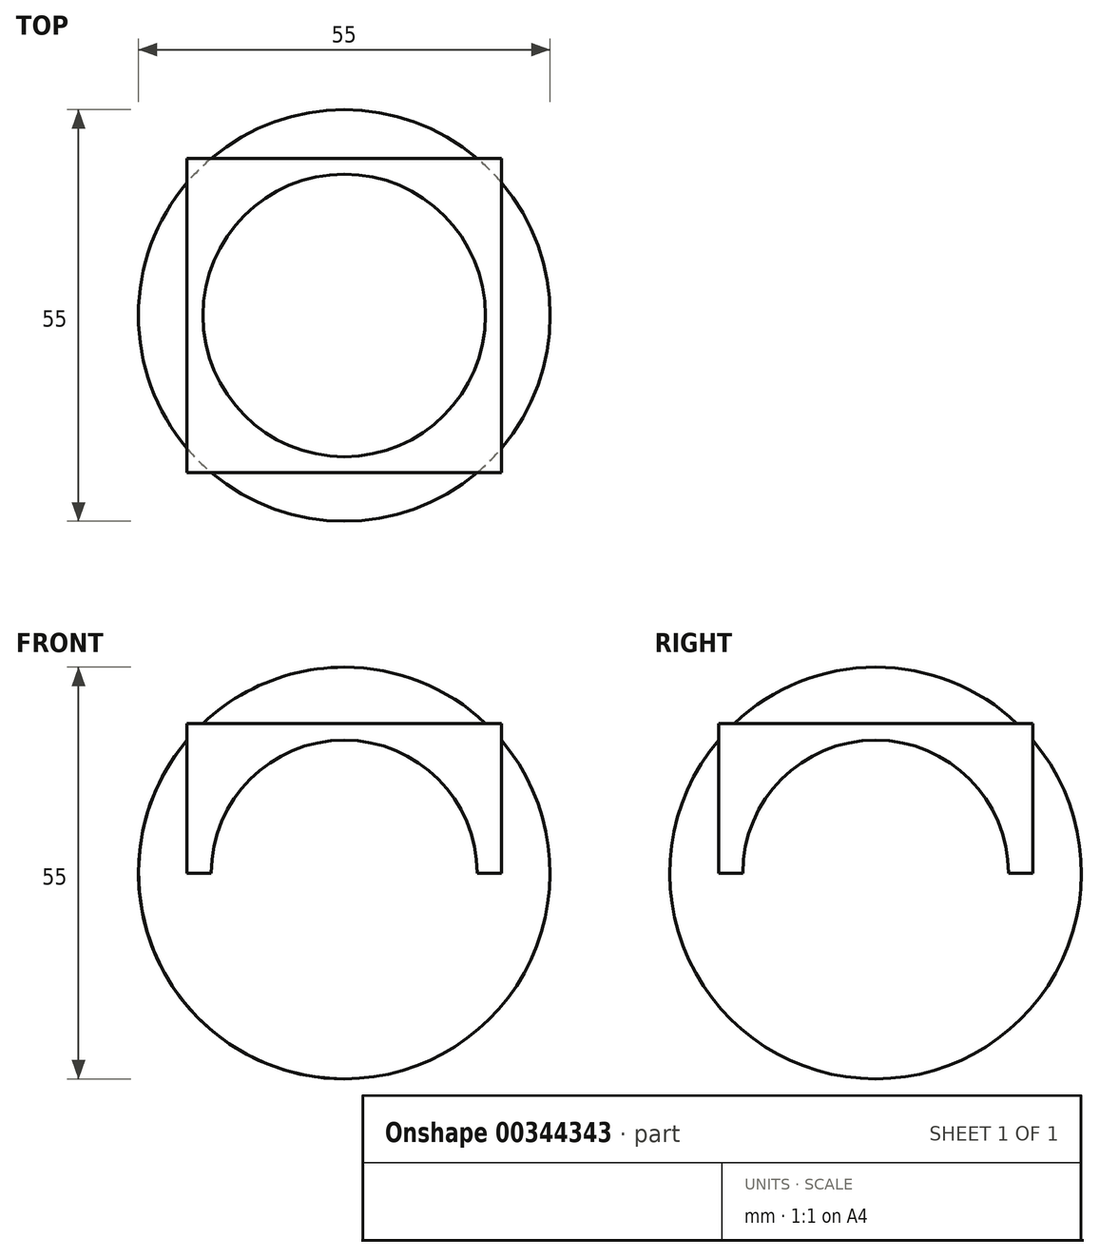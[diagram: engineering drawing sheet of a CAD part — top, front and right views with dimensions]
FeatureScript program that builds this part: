
annotation { "Feature Type Name" : "Feature", "Feature Type Description" : "" }
export const myFeature = defineFeature(function(context is Context, id is Id, definition is map)
    precondition{}
    {
        {
            var Q0;
            Q0=qCreatedBy(makeId("Front.planeOp"),FACE);
            var sketch = newSketch(context, id + "F0", { "sketchPlane" : qUnion([Q0])});
            skCircle(sketch, "E0", {"center": v(0, 0) * mm, "radius": 27.5 * mm});
            skLineSegment(sketch, "E1", {"start": v(0, -40.1) * mm, "end": v(0, 41.32) * mm});
            skSolve(sketch);
        }
        {
            var Q0;
            {var subQ0=sQuery(id+"F0.wireOp",EDGE,"E1");var subQ1=sQuery(id+"F0.wireOp",EDGE,"E0");var subQ2=makeQuery(id+"F0.imprint","INTERSECT",VERTEX,{"disambiguationData":[OD(0.0)],"derivedFrom":[subQ1,subQ0]});Q0=makeQuery(id+"F0.imprint","IMPRINT",FACE,{"disambiguationData":[TD([[makeQuery(id+"F0.imprint","IMPRINT",EDGE,{"disambiguationData":[TD([[subQ2,1.0]])],"derivedFrom":subQ1}),1.0]])]});}
            var Q1;
            Q1=sQuery(id+"F0.wireOp",EDGE,"E1");
            revolve(context, id + "F1", {"entities" : qUnion([Q0]), "axis" : qUnion([Q1]), "revolveType" : RevolveType.FULL});
        }
        {
            var Q0;
            Q0=qCreatedBy(makeId("Top.planeOp"),FACE);
            var sketch = newSketch(context, id + "F2", { "sketchPlane" : qUnion([Q0])});
            skLineSegment(sketch, "E2.bottom", {"start": v(21, -21) * mm, "end": v(-21, -21) * mm});
            skLineSegment(sketch, "E2.top", {"start": v(21, 21) * mm, "end": v(-21, 21) * mm});
            skLineSegment(sketch, "E2.left", {"start": v(21, -21) * mm, "end": v(21, 21) * mm});
            skLineSegment(sketch, "E2.right", {"start": v(-21, -21) * mm, "end": v(-21, 21) * mm});
            skPoint(sketch, "E2.middle", {"position": v(0, 0) * mm});
            skSolve(sketch);
        }
        {
            var Q0;
            Q0=makeQuery(id+"F2.imprint","IMPRINT",FACE,{"disambiguationData":[TD([[makeQuery(id+"F2.imprint","IMPRINT",EDGE,{"derivedFrom":sQuery(id+"F2.wireOp",EDGE,"E2.bottom")}),-1.0]])]});
            extrude(context, id + "F3", {"entities" : qUnion([Q0]), "operationType" : NewBodyOperationType.ADD, "depth" : 20 * mm});
        }
    });
